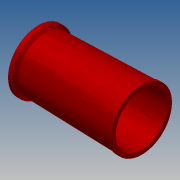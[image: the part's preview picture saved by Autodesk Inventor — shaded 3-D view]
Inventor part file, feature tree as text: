
AUTODESK INVENTOR PART (.ipt)
format: ipt  version: 2017.3 (Build 213257000, 257)  size: 163,328 bytes
history: native  units: in
note: dims shown in document units (in); Inventor stores cm internally (conversion verified against a paired STEP export)
features: other x3, extrude x2, sketch x2, chamfer x1
ambient origin geometry x8: Origin, YZ Plane, XZ Plane, XY Plane, X Axis, Y Axis, Z Axis, Center Point
bodies: Solid1 (feature_tree)
feature tree (8):
  other  "A1-19027-200-04 HCWi reducer.ipt"
  extrude  "Extrusion1"  Depth=0.5in TaperAngle=0.0deg
  extrude  "Extrusion2"  Depth=0.5in
  chamfer  "Chamfer1"  Distance=0.25in Angle=45.0deg
  other  "Solid1::A1-19027-200-04 HCWi reducer.ipt"
  other  "TaggingFeature1"
  sketch  "Sketch2"  dims[d0=0.3937in d1=0.5in d2=2.0in d3=0.0in d4=0.0in]
  sketch  "Sketch3"  dims[d5=0.5in d6=2.0in d7=0.0in d8=0.0in d9=0.25in d10=0.25in d11=0.125in d12=45.0deg d13=0.25in]
